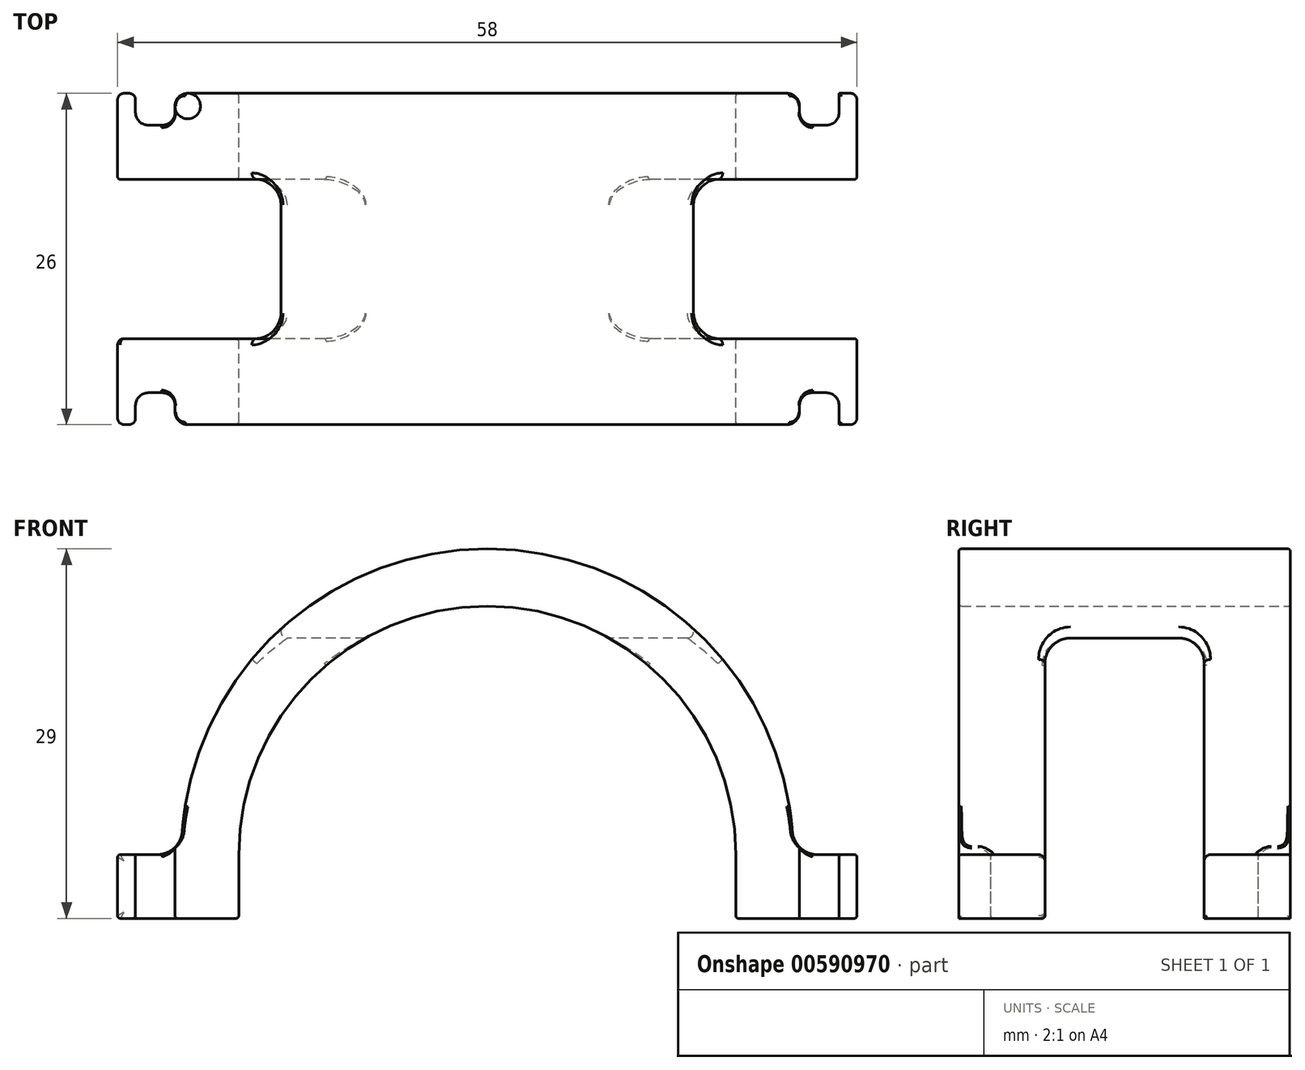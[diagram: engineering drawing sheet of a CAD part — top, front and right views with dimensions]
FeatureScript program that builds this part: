
annotation { "Feature Type Name" : "Feature", "Feature Type Description" : "" }
export const myFeature = defineFeature(function(context is Context, id is Id, definition is map)
    precondition{}
    {
        {
            var Q0;
            Q0=qCreatedBy(makeId("Front.planeOp"),FACE);
            var sketch = newSketch(context, id + "F0", { "sketchPlane" : qUnion([Q0])});
            skArc(sketch, "E0", {"start": v(19.5, 0) * mm, "mid": v(0, 19.5) * mm, "end": v(-19.5, 0) * mm});
            skArc(sketch, "E1", {"start": v(24, 0) * mm, "mid": v(0, 24) * mm, "end": v(-24, 0) * mm});
            skLineSegment(sketch, "E2", {"start": v(-24, 0) * mm, "end": v(24, 0) * mm, "construction": true});
            skLineSegment(sketch, "E3.0", {"start": v(-24, -5) * mm, "end": v(-19.5, -5) * mm});
            skLineSegment(sketch, "E4", {"start": v(-19.5, 0) * mm, "end": v(-19.5, -5) * mm});
            skLineSegment(sketch, "E5", {"start": v(19.5, 0) * mm, "end": v(19.5, -5) * mm});
            skLineSegment(sketch, "E6.trimOffspring", {"start": v(19.5, -5) * mm, "end": v(24, -5) * mm});
            skLineSegment(sketch, "E7", {"start": v(-24, -5) * mm, "end": v(-29, -5) * mm});
            skLineSegment(sketch, "E8", {"start": v(-29, -5) * mm, "end": v(-29, 0) * mm});
            skLineSegment(sketch, "E9", {"start": v(-29, 0) * mm, "end": v(-24, 0) * mm});
            skLineSegment(sketch, "E10.MirrorCS", {"start": v(29, 0) * mm, "end": v(24, 0) * mm});
            skLineSegment(sketch, "E11.MirrorCS", {"start": v(29, -5) * mm, "end": v(29, 0) * mm});
            skLineSegment(sketch, "E12.MirrorCS", {"start": v(24, -5) * mm, "end": v(29, -5) * mm});
            skSolve(sketch);
        }
        {
            var Q0;
            Q0 = qSketchRegion(id + "F0", true);
            extrude(context, id + "F1", {"entities" : qUnion([Q0]), "depth" : 26 * mm, "offsetDistance" : 25 * mm});
        }
        {
            var Q0;
            Q0=makeQuery(id+"F1.opExtrude","SWEPT_FACE",FACE,{"disambiguationData":[OSD([sQuery(id+"F0.wireOp",EDGE,"E9")])]});
            var sketch = newSketch(context, id + "F2", { "sketchPlane" : qUnion([Q0])});
            skLineSegment(sketch, "E13.0", {"start": v(-27.6, -26) * mm, "end": v(-27.6, -23.5) * mm});
            skLineSegment(sketch, "E14.0", {"start": v(-24.5, -26) * mm, "end": v(-24.5, -23.5) * mm});
            skLineSegment(sketch, "E15.0", {"start": v(-27.6, -2.5) * mm, "end": v(-24.5, -2.5) * mm});
            skLineSegment(sketch, "E16", {"start": v(-24, -13) * mm, "end": v(-34.7, -13) * mm, "construction": true});
            skLineSegment(sketch, "E17.MirrorCS", {"start": v(-27.6, -23.5) * mm, "end": v(-24.5, -23.5) * mm});
            skPoint(sketch, "E18.orphan", {"position": v(-29, -2.5) * mm});
            skLineSegment(sketch, "E19.trimOffspring", {"start": v(-27.6, -2.5) * mm, "end": v(-27.6, 0) * mm});
            skPoint(sketch, "E20.orphan", {"position": v(-29, -23.5) * mm});
            skPoint(sketch, "E21.orphan", {"position": v(-24, -23.5) * mm});
            skLineSegment(sketch, "E22.trimOffspring", {"start": v(-24.5, -2.5) * mm, "end": v(-24.5, 0) * mm});
            skLineSegment(sketch, "E23", {"start": v(0, 0) * mm, "end": v(0, -26.74) * mm, "construction": true});
            skLineSegment(sketch, "E24.MirrorCS", {"start": v(27.6, -2.5) * mm, "end": v(24, -2.5) * mm});
            skLineSegment(sketch, "E25.MirrorCS", {"start": v(24.5, -2.5) * mm, "end": v(24.5, 0) * mm});
            skLineSegment(sketch, "E26.MirrorCS", {"start": v(27.6, -2.5) * mm, "end": v(27.6, 0) * mm});
            skLineSegment(sketch, "E27.MirrorCS", {"start": v(27.6, -26) * mm, "end": v(27.6, -23.5) * mm});
            skLineSegment(sketch, "E28.MirrorCS", {"start": v(27.6, -23.5) * mm, "end": v(24.5, -23.5) * mm});
            skLineSegment(sketch, "E29.MirrorCS", {"start": v(24.5, -26) * mm, "end": v(24.5, -23.5) * mm});
            skPoint(sketch, "E30.orphan", {"position": v(-24, -2.5) * mm});
            skLineSegment(sketch, "E31", {"start": v(-27.6, -26) * mm, "end": v(-24.5, -26) * mm});
            skLineSegment(sketch, "E32", {"start": v(-27.6, 0) * mm, "end": v(-24.5, 0) * mm});
            skLineSegment(sketch, "E33", {"start": v(24.5, 0) * mm, "end": v(27.6, 0) * mm});
            skLineSegment(sketch, "E34", {"start": v(27.6, -26) * mm, "end": v(24.5, -26) * mm});
            skSolve(sketch);
        }
        {
            var Q0;
            Q0 = qSketchRegion(id + "F2", true);
            var Q1;
            Q1=makeQuery(id+"F1.opExtrude","SWEPT_FACE",FACE,{"disambiguationData":[OSD([sQuery(id+"F0.wireOp",EDGE,"E6.trimOffspring"),sQuery(id+"F0.wireOp",EDGE,"E12.MirrorCS")])]});
            extrude(context, id + "F3", {"entities" : qUnion([Q0]), "operationType" : NewBodyOperationType.REMOVE, "endBound" : BoundingType.UP_TO_SURFACE, "oppositeDirection" : true, "depth" : 25 * mm, "endBoundEntityFace" : qUnion([Q1]), "offsetDistance" : 25 * mm});
        }
        {
            var Q0;
            Q0=makeQuery(id+"F1.opExtrude","SWEPT_FACE",FACE,{"disambiguationData":[OSD([sQuery(id+"F0.wireOp",EDGE,"E8")])]});
            var sketch = newSketch(context, id + "F4", { "sketchPlane" : qUnion([Q0])});
            skLineSegment(sketch, "E35", {"start": v(13, -5) * mm, "end": v(13, 34.64) * mm, "construction": true});
            skLineSegment(sketch, "E36.0", {"start": v(19.25, -5) * mm, "end": v(19.25, 17) * mm});
            skLineSegment(sketch, "E37.0", {"start": v(19.25, 17) * mm, "end": v(6.75, 17) * mm});
            skLineSegment(sketch, "E38.MirrorCS", {"start": v(6.75, -5) * mm, "end": v(6.75, 17) * mm});
            skLineSegment(sketch, "E39", {"start": v(6.75, -5) * mm, "end": v(19.25, -5) * mm});
            skSolve(sketch);
        }
        {
            var Q0;
            Q0 = qSketchRegion(id + "F4", true);
            extrude(context, id + "F5", {"entities" : qUnion([Q0]), "operationType" : NewBodyOperationType.REMOVE, "endBound" : BoundingType.THROUGH_ALL, "oppositeDirection" : true, "depth" : 25 * mm, "offsetDistance" : 25 * mm});
        }
        {
            var Q0;
            Q0=makeQuery(id+"F3.boolean.opBoolean","COPY",EDGE,{"derivedFrom":makeQuery(id+"F3.opExtrude","SWEPT_EDGE",EDGE,{"disambiguationData":[OSD([sQuery(id+"F2.wireOp",EDGE,"E14.0"),sQuery(id+"F2.wireOp",EDGE,"E17.MirrorCS")])]})});
            var Q1;
            Q1=makeQuery(id+"F3.boolean.opBoolean","COPY",EDGE,{"derivedFrom":makeQuery(id+"F3.opExtrude","SWEPT_EDGE",EDGE,{"disambiguationData":[OSD([sQuery(id+"F2.wireOp",EDGE,"E13.0"),sQuery(id+"F2.wireOp",EDGE,"E17.MirrorCS")])]})});
            var Q2;
            Q2=makeQuery(id+"F3.boolean.opBoolean","COPY",EDGE,{"derivedFrom":makeQuery(id+"F3.opExtrude","SWEPT_EDGE",EDGE,{"disambiguationData":[OSD([sQuery(id+"F2.wireOp",EDGE,"E28.MirrorCS"),sQuery(id+"F2.wireOp",EDGE,"E29.MirrorCS")])]})});
            var Q3;
            Q3=makeQuery(id+"F3.boolean.opBoolean","COPY",EDGE,{"derivedFrom":makeQuery(id+"F3.opExtrude","SWEPT_EDGE",EDGE,{"disambiguationData":[OSD([sQuery(id+"F2.wireOp",EDGE,"E27.MirrorCS"),sQuery(id+"F2.wireOp",EDGE,"E28.MirrorCS")])]})});
            var Q4;
            Q4=makeQuery(id+"F3.boolean.opBoolean","COPY",EDGE,{"derivedFrom":makeQuery(id+"F3.opExtrude","SWEPT_EDGE",EDGE,{"disambiguationData":[OSD([sQuery(id+"F2.wireOp",EDGE,"E15.0"),sQuery(id+"F2.wireOp",EDGE,"E22.trimOffspring")])]})});
            var Q5;
            Q5=makeQuery(id+"F3.boolean.opBoolean","COPY",EDGE,{"derivedFrom":makeQuery(id+"F3.opExtrude","SWEPT_EDGE",EDGE,{"disambiguationData":[OSD([sQuery(id+"F2.wireOp",EDGE,"E24.MirrorCS"),sQuery(id+"F2.wireOp",EDGE,"E26.MirrorCS")])]})});
            var Q6;
            Q6=makeQuery(id+"F3.boolean.opBoolean","COPY",EDGE,{"derivedFrom":makeQuery(id+"F3.opExtrude","SWEPT_EDGE",EDGE,{"disambiguationData":[OSD([sQuery(id+"F2.wireOp",EDGE,"E15.0"),sQuery(id+"F2.wireOp",EDGE,"E19.trimOffspring")])]})});
            var Q7;
            Q7=makeQuery(id+"F3.boolean.opBoolean","COPY",EDGE,{"derivedFrom":makeQuery(id+"F3.opExtrude","SWEPT_EDGE",EDGE,{"disambiguationData":[OSD([sQuery(id+"F2.wireOp",EDGE,"E24.MirrorCS"),sQuery(id+"F2.wireOp",EDGE,"E25.MirrorCS")])]})});
            var Q8;
            Q8=makeQuery(id+"F3.boolean.opBoolean","COPY",EDGE,{"derivedFrom":makeQuery(id+"F3.opExtrude","SWEPT_EDGE",EDGE,{"disambiguationData":[OSD([sQuery(id+"F0.wireOp",EDGE,"E9"),sQuery(id+"F2.wireOp",EDGE,"E14.0"),sQuery(id+"F2.wireOp",EDGE,"E31")])]})});
            var Q9;
            Q9=makeQuery(id+"F3.boolean.opBoolean","COPY",EDGE,{"derivedFrom":makeQuery(id+"F3.opExtrude","SWEPT_EDGE",EDGE,{"disambiguationData":[OSD([sQuery(id+"F0.wireOp",EDGE,"E9"),sQuery(id+"F2.wireOp",EDGE,"E22.trimOffspring"),sQuery(id+"F2.wireOp",EDGE,"E32")])]})});
            var Q10;
            Q10=makeQuery(id+"F3.boolean.opBoolean","COPY",EDGE,{"derivedFrom":makeQuery(id+"F3.opExtrude","SWEPT_EDGE",EDGE,{"disambiguationData":[OSD([sQuery(id+"F2.wireOp",EDGE,"E29.MirrorCS"),sQuery(id+"F2.wireOp",EDGE,"E34")])]})});
            var Q11;
            Q11=makeQuery(id+"F3.boolean.opBoolean","COPY",EDGE,{"derivedFrom":makeQuery(id+"F3.opExtrude","SWEPT_EDGE",EDGE,{"disambiguationData":[OSD([sQuery(id+"F2.wireOp",EDGE,"E25.MirrorCS"),sQuery(id+"F2.wireOp",EDGE,"E33")])]})});
            fillet(context, id + "F6", {"entities" : qUnion([Q0, Q1, Q2, Q3, Q4, Q5, Q6, Q7, Q8, Q9, Q10, Q11]), "radius" : 1 * mm, "tangentPropagation" : true, "allowEdgeOverflow" : false});
        }
        {
            var Q0;
            Q0=makeQuery(id+"F3.boolean.opBoolean","COPY",EDGE,{"derivedFrom":makeQuery(id+"F3.opExtrude","SWEPT_EDGE",EDGE,{"disambiguationData":[OSD([sQuery(id+"F2.wireOp",EDGE,"E26.MirrorCS"),sQuery(id+"F2.wireOp",EDGE,"E33")])]})});
            var Q1;
            Q1=makeQuery(id+"F1.opExtrude","CAP_EDGE",EDGE,{"disambiguationData":[OSD([sQuery(id+"F0.wireOp",EDGE,"E11.MirrorCS")])],"isStart":true});
            var Q2;
            Q2=makeQuery(id+"F1.opExtrude","CAP_EDGE",EDGE,{"disambiguationData":[OSD([sQuery(id+"F0.wireOp",EDGE,"E11.MirrorCS")])],"isStart":false});
            var Q3;
            Q3=makeQuery(id+"F3.boolean.opBoolean","COPY",EDGE,{"derivedFrom":makeQuery(id+"F3.opExtrude","SWEPT_EDGE",EDGE,{"disambiguationData":[OSD([sQuery(id+"F2.wireOp",EDGE,"E27.MirrorCS"),sQuery(id+"F2.wireOp",EDGE,"E34")])]})});
            var Q4;
            Q4=makeQuery(id+"F3.boolean.opBoolean","COPY",EDGE,{"derivedFrom":makeQuery(id+"F3.opExtrude","SWEPT_EDGE",EDGE,{"disambiguationData":[OSD([sQuery(id+"F0.wireOp",EDGE,"E9"),sQuery(id+"F2.wireOp",EDGE,"E13.0"),sQuery(id+"F2.wireOp",EDGE,"E31")])]})});
            var Q5;
            Q5=makeQuery(id+"F1.opExtrude","CAP_EDGE",EDGE,{"disambiguationData":[OSD([sQuery(id+"F0.wireOp",EDGE,"E8")])],"isStart":false});
            var Q6;
            Q6=makeQuery(id+"F1.opExtrude","CAP_EDGE",EDGE,{"disambiguationData":[OSD([sQuery(id+"F0.wireOp",EDGE,"E8")])],"isStart":true});
            var Q7;
            Q7=makeQuery(id+"F3.boolean.opBoolean","COPY",EDGE,{"derivedFrom":makeQuery(id+"F3.opExtrude","SWEPT_EDGE",EDGE,{"disambiguationData":[OSD([sQuery(id+"F0.wireOp",EDGE,"E9"),sQuery(id+"F2.wireOp",EDGE,"E19.trimOffspring"),sQuery(id+"F2.wireOp",EDGE,"E32")])]})});
            fillet(context, id + "F7", {"entities" : qUnion([Q0, Q1, Q2, Q3, Q4, Q5, Q6, Q7]), "radius" : 0.5 * mm, "tangentPropagation" : true, "allowEdgeOverflow" : false});
        }
        {
            var Q0;
            {var subQ0=sQuery(id+"F0.wireOp",EDGE,"E10.MirrorCS");var subQ1=sQuery(id+"F0.wireOp",EDGE,"E1");Q0=makeQuery(id+"F5.boolean.opBoolean","SPLIT",EDGE,{"disambiguationData":[TD([makeQuery(id+"F5.opExtrude","SWEPT_FACE",FACE,{"disambiguationData":[OSD([sQuery(id+"F4.wireOp",EDGE,"E36.0")])]})])],"derivedFrom":makeQuery(id+"F1.opExtrude","SWEPT_EDGE",EDGE,{"disambiguationData":[OSD([subQ1,subQ0])]})});}
            var Q1;
            {var subQ0=sQuery(id+"F0.wireOp",EDGE,"E10.MirrorCS");var subQ1=sQuery(id+"F0.wireOp",EDGE,"E1");Q1=makeQuery(id+"F5.boolean.opBoolean","SPLIT",EDGE,{"disambiguationData":[TD([makeQuery(id+"F5.opExtrude","SWEPT_FACE",FACE,{"disambiguationData":[OSD([sQuery(id+"F4.wireOp",EDGE,"E38.MirrorCS")])]})])],"derivedFrom":makeQuery(id+"F1.opExtrude","SWEPT_EDGE",EDGE,{"disambiguationData":[OSD([subQ1,subQ0])]})});}
            var Q2;
            {var subQ0=sQuery(id+"F0.wireOp",EDGE,"E9");var subQ1=sQuery(id+"F0.wireOp",EDGE,"E1");Q2=makeQuery(id+"F5.boolean.opBoolean","SPLIT",EDGE,{"disambiguationData":[TD([makeQuery(id+"F5.opExtrude","SWEPT_FACE",FACE,{"disambiguationData":[OSD([sQuery(id+"F4.wireOp",EDGE,"E36.0")])]})])],"derivedFrom":makeQuery(id+"F1.opExtrude","SWEPT_EDGE",EDGE,{"disambiguationData":[OSD([subQ1,subQ0])]})});}
            var Q3;
            {var subQ0=sQuery(id+"F0.wireOp",EDGE,"E9");var subQ1=sQuery(id+"F0.wireOp",EDGE,"E1");Q3=makeQuery(id+"F5.boolean.opBoolean","SPLIT",EDGE,{"disambiguationData":[TD([makeQuery(id+"F5.opExtrude","SWEPT_FACE",FACE,{"disambiguationData":[OSD([sQuery(id+"F4.wireOp",EDGE,"E38.MirrorCS")])]})])],"derivedFrom":makeQuery(id+"F1.opExtrude","SWEPT_EDGE",EDGE,{"disambiguationData":[OSD([subQ1,subQ0])]})});}
            var Q4;
            Q4=makeQuery(id+"F5.boolean.opBoolean","COPY",EDGE,{"disambiguationData":[OD(1.0)],"derivedFrom":makeQuery(id+"F5.opExtrude","SWEPT_EDGE",EDGE,{"disambiguationData":[OSD([sQuery(id+"F4.wireOp",EDGE,"E36.0"),sQuery(id+"F4.wireOp",EDGE,"E37.0")])]})});
            var Q5;
            Q5=makeQuery(id+"F5.boolean.opBoolean","COPY",EDGE,{"disambiguationData":[OD(1.0)],"derivedFrom":makeQuery(id+"F5.opExtrude","SWEPT_EDGE",EDGE,{"disambiguationData":[OSD([sQuery(id+"F4.wireOp",EDGE,"E37.0"),sQuery(id+"F4.wireOp",EDGE,"E38.MirrorCS")])]})});
            var Q6;
            Q6=makeQuery(id+"F5.boolean.opBoolean","COPY",EDGE,{"disambiguationData":[OD(0.0)],"derivedFrom":makeQuery(id+"F5.opExtrude","SWEPT_EDGE",EDGE,{"disambiguationData":[OSD([sQuery(id+"F4.wireOp",EDGE,"E37.0"),sQuery(id+"F4.wireOp",EDGE,"E38.MirrorCS")])]})});
            var Q7;
            Q7=makeQuery(id+"F5.boolean.opBoolean","COPY",EDGE,{"disambiguationData":[OD(0.0)],"derivedFrom":makeQuery(id+"F5.opExtrude","SWEPT_EDGE",EDGE,{"disambiguationData":[OSD([sQuery(id+"F4.wireOp",EDGE,"E36.0"),sQuery(id+"F4.wireOp",EDGE,"E37.0")])]})});
            fillet(context, id + "F8", {"entities" : qUnion([Q0, Q1, Q2, Q3, Q4, Q5, Q6, Q7]), "radius" : 2 * mm, "tangentPropagation" : true, "allowEdgeOverflow" : false});
        }
        {
            var Q0;
            Q0=makeQuery(id+"F5.boolean.opBoolean","INTERSECT",EDGE,{"derivedFrom":[makeQuery(id+"F1.opExtrude","SWEPT_FACE",FACE,{"disambiguationData":[OSD([sQuery(id+"F0.wireOp",EDGE,"E11.MirrorCS")])]}),makeQuery(id+"F5.opExtrude","SWEPT_FACE",FACE,{"disambiguationData":[OSD([sQuery(id+"F4.wireOp",EDGE,"E36.0")])]})]});
            var Q1;
            Q1=makeQuery(id+"F5.boolean.opBoolean","INTERSECT",EDGE,{"derivedFrom":[makeQuery(id+"F1.opExtrude","SWEPT_FACE",FACE,{"disambiguationData":[OSD([sQuery(id+"F0.wireOp",EDGE,"E11.MirrorCS")])]}),makeQuery(id+"F5.opExtrude","SWEPT_FACE",FACE,{"disambiguationData":[OSD([sQuery(id+"F4.wireOp",EDGE,"E38.MirrorCS")])]})]});
            var Q2;
            {var subQ0=sQuery(id+"F4.wireOp",EDGE,"E38.MirrorCS");Q2=makeQuery(id+"F5.boolean.opBoolean","COPY",EDGE,{"disambiguationData":[topologyDisambiguationEdgeConnected([makeQuery(id+"F1.opExtrude","SWEPT_FACE",FACE,{"disambiguationData":[OSD([sQuery(id+"F0.wireOp",EDGE,"E6.trimOffspring"),sQuery(id+"F0.wireOp",EDGE,"E12.MirrorCS")])]})])],"derivedFrom":makeQuery(id+"F5.opExtrude","SWEPT_EDGE",EDGE,{"disambiguationData":[OSD([sQuery(id+"F0.wireOp",EDGE,"E7"),sQuery(id+"F0.wireOp",EDGE,"E8"),subQ0,sQuery(id+"F4.wireOp",EDGE,"E39")])]})});}
            var Q3;
            {var subQ0=sQuery(id+"F4.wireOp",EDGE,"E36.0");Q3=makeQuery(id+"F5.boolean.opBoolean","COPY",EDGE,{"disambiguationData":[topologyDisambiguationEdgeConnected([makeQuery(id+"F1.opExtrude","SWEPT_FACE",FACE,{"disambiguationData":[OSD([sQuery(id+"F0.wireOp",EDGE,"E6.trimOffspring"),sQuery(id+"F0.wireOp",EDGE,"E12.MirrorCS")])]})])],"derivedFrom":makeQuery(id+"F5.opExtrude","SWEPT_EDGE",EDGE,{"disambiguationData":[OSD([sQuery(id+"F0.wireOp",EDGE,"E7"),sQuery(id+"F0.wireOp",EDGE,"E8"),subQ0,sQuery(id+"F4.wireOp",EDGE,"E39")])]})});}
            var Q4;
            Q4=makeQuery(id+"F5.boolean.opBoolean","COPY",EDGE,{"derivedFrom":makeQuery(id+"F5.opExtrude","CAP_EDGE",EDGE,{"disambiguationData":[OSD([sQuery(id+"F4.wireOp",EDGE,"E38.MirrorCS")])],"isStart":true})});
            var Q5;
            Q5=makeQuery(id+"F5.boolean.opBoolean","COPY",EDGE,{"derivedFrom":makeQuery(id+"F5.opExtrude","CAP_EDGE",EDGE,{"disambiguationData":[OSD([sQuery(id+"F4.wireOp",EDGE,"E36.0")])],"isStart":true})});
            var Q6;
            {var subQ0=sQuery(id+"F0.wireOp",EDGE,"E7");var subQ1=sQuery(id+"F4.wireOp",EDGE,"E38.MirrorCS");Q6=makeQuery(id+"F5.boolean.opBoolean","COPY",EDGE,{"disambiguationData":[topologyDisambiguationEdgeConnected([makeQuery(id+"F1.opExtrude","SWEPT_FACE",FACE,{"disambiguationData":[OSD([sQuery(id+"F0.wireOp",EDGE,"E3.0"),subQ0])]})])],"derivedFrom":makeQuery(id+"F5.opExtrude","SWEPT_EDGE",EDGE,{"disambiguationData":[OSD([subQ0,sQuery(id+"F0.wireOp",EDGE,"E8"),subQ1,sQuery(id+"F4.wireOp",EDGE,"E39")])]})});}
            var Q7;
            {var subQ0=sQuery(id+"F0.wireOp",EDGE,"E7");var subQ1=sQuery(id+"F4.wireOp",EDGE,"E36.0");Q7=makeQuery(id+"F5.boolean.opBoolean","COPY",EDGE,{"disambiguationData":[topologyDisambiguationEdgeConnected([makeQuery(id+"F1.opExtrude","SWEPT_FACE",FACE,{"disambiguationData":[OSD([sQuery(id+"F0.wireOp",EDGE,"E3.0"),subQ0])]})])],"derivedFrom":makeQuery(id+"F5.opExtrude","SWEPT_EDGE",EDGE,{"disambiguationData":[OSD([subQ0,sQuery(id+"F0.wireOp",EDGE,"E8"),subQ1,sQuery(id+"F4.wireOp",EDGE,"E39")])]})});}
            var Q8;
            {var subQ0=sQuery(id+"F0.wireOp",EDGE,"E9");var subQ1=sQuery(id+"F0.wireOp",EDGE,"E8");Q8=makeQuery(id+"F5.boolean.opBoolean","SPLIT",EDGE,{"disambiguationData":[TD([makeQuery(id+"F5.opExtrude","SWEPT_FACE",FACE,{"disambiguationData":[OSD([sQuery(id+"F4.wireOp",EDGE,"E38.MirrorCS")])]})])],"derivedFrom":makeQuery(id+"F1.opExtrude","SWEPT_EDGE",EDGE,{"disambiguationData":[OSD([subQ1,subQ0])]})});}
            var Q9;
            {var subQ0=sQuery(id+"F0.wireOp",EDGE,"E9");var subQ1=sQuery(id+"F0.wireOp",EDGE,"E8");Q9=makeQuery(id+"F5.boolean.opBoolean","SPLIT",EDGE,{"disambiguationData":[TD([makeQuery(id+"F5.opExtrude","SWEPT_FACE",FACE,{"disambiguationData":[OSD([sQuery(id+"F4.wireOp",EDGE,"E36.0")])]})])],"derivedFrom":makeQuery(id+"F1.opExtrude","SWEPT_EDGE",EDGE,{"disambiguationData":[OSD([subQ1,subQ0])]})});}
            var Q10;
            {var subQ0=sQuery(id+"F0.wireOp",EDGE,"E8");var subQ1=sQuery(id+"F0.wireOp",EDGE,"E7");Q10=makeQuery(id+"F5.boolean.opBoolean","SPLIT",EDGE,{"disambiguationData":[TD([makeQuery(id+"F5.opExtrude","SWEPT_FACE",FACE,{"disambiguationData":[OSD([sQuery(id+"F4.wireOp",EDGE,"E38.MirrorCS")])]})])],"derivedFrom":makeQuery(id+"F1.opExtrude","SWEPT_EDGE",EDGE,{"disambiguationData":[OSD([subQ1,subQ0])]})});}
            var Q11;
            {var subQ0=sQuery(id+"F0.wireOp",EDGE,"E8");var subQ1=sQuery(id+"F0.wireOp",EDGE,"E7");Q11=makeQuery(id+"F5.boolean.opBoolean","SPLIT",EDGE,{"disambiguationData":[TD([makeQuery(id+"F5.opExtrude","SWEPT_FACE",FACE,{"disambiguationData":[OSD([sQuery(id+"F4.wireOp",EDGE,"E36.0")])]})])],"derivedFrom":makeQuery(id+"F1.opExtrude","SWEPT_EDGE",EDGE,{"disambiguationData":[OSD([subQ1,subQ0])]})});}
            var Q12;
            {var subQ1=sQuery(id+"F0.wireOp",EDGE,"E4");var subQ2=sQuery(id+"F0.wireOp",EDGE,"E3.0");Q12=makeQuery(id+"F5.boolean.opBoolean","SPLIT",EDGE,{"disambiguationData":[TD([makeQuery(id+"F5.opExtrude","SWEPT_FACE",FACE,{"disambiguationData":[OSD([sQuery(id+"F4.wireOp",EDGE,"E38.MirrorCS")])]})])],"derivedFrom":makeQuery(id+"F1.opExtrude","SWEPT_EDGE",EDGE,{"disambiguationData":[OSD([subQ2,subQ1])]})});}
            var Q13;
            {var subQ1=sQuery(id+"F0.wireOp",EDGE,"E4");var subQ2=sQuery(id+"F0.wireOp",EDGE,"E3.0");Q13=makeQuery(id+"F5.boolean.opBoolean","SPLIT",EDGE,{"disambiguationData":[TD([makeQuery(id+"F5.opExtrude","SWEPT_FACE",FACE,{"disambiguationData":[OSD([sQuery(id+"F4.wireOp",EDGE,"E36.0")])]})])],"derivedFrom":makeQuery(id+"F1.opExtrude","SWEPT_EDGE",EDGE,{"disambiguationData":[OSD([subQ2,subQ1])]})});}
            var Q14;
            {var subQ1=sQuery(id+"F0.wireOp",EDGE,"E6.trimOffspring");var subQ2=sQuery(id+"F0.wireOp",EDGE,"E5");Q14=makeQuery(id+"F5.boolean.opBoolean","SPLIT",EDGE,{"disambiguationData":[TD([makeQuery(id+"F5.opExtrude","SWEPT_FACE",FACE,{"disambiguationData":[OSD([sQuery(id+"F4.wireOp",EDGE,"E38.MirrorCS")])]})])],"derivedFrom":makeQuery(id+"F1.opExtrude","SWEPT_EDGE",EDGE,{"disambiguationData":[OSD([subQ2,subQ1])]})});}
            var Q15;
            {var subQ0=sQuery(id+"F0.wireOp",EDGE,"E12.MirrorCS");var subQ1=sQuery(id+"F0.wireOp",EDGE,"E11.MirrorCS");Q15=makeQuery(id+"F5.boolean.opBoolean","SPLIT",EDGE,{"disambiguationData":[TD([makeQuery(id+"F5.opExtrude","SWEPT_FACE",FACE,{"disambiguationData":[OSD([sQuery(id+"F4.wireOp",EDGE,"E38.MirrorCS")])]})])],"derivedFrom":makeQuery(id+"F1.opExtrude","SWEPT_EDGE",EDGE,{"disambiguationData":[OSD([subQ1,subQ0])]})});}
            var Q16;
            {var subQ0=sQuery(id+"F0.wireOp",EDGE,"E12.MirrorCS");var subQ1=sQuery(id+"F0.wireOp",EDGE,"E11.MirrorCS");Q16=makeQuery(id+"F5.boolean.opBoolean","SPLIT",EDGE,{"disambiguationData":[TD([makeQuery(id+"F5.opExtrude","SWEPT_FACE",FACE,{"disambiguationData":[OSD([sQuery(id+"F4.wireOp",EDGE,"E36.0")])]})])],"derivedFrom":makeQuery(id+"F1.opExtrude","SWEPT_EDGE",EDGE,{"disambiguationData":[OSD([subQ1,subQ0])]})});}
            var Q17;
            {var subQ1=sQuery(id+"F0.wireOp",EDGE,"E6.trimOffspring");var subQ2=sQuery(id+"F0.wireOp",EDGE,"E5");Q17=makeQuery(id+"F5.boolean.opBoolean","SPLIT",EDGE,{"disambiguationData":[TD([makeQuery(id+"F5.opExtrude","SWEPT_FACE",FACE,{"disambiguationData":[OSD([sQuery(id+"F4.wireOp",EDGE,"E36.0")])]})])],"derivedFrom":makeQuery(id+"F1.opExtrude","SWEPT_EDGE",EDGE,{"disambiguationData":[OSD([subQ2,subQ1])]})});}
            var Q18;
            {var subQ0=sQuery(id+"F0.wireOp",EDGE,"E11.MirrorCS");var subQ1=sQuery(id+"F0.wireOp",EDGE,"E10.MirrorCS");Q18=makeQuery(id+"F5.boolean.opBoolean","SPLIT",EDGE,{"disambiguationData":[TD([makeQuery(id+"F5.opExtrude","SWEPT_FACE",FACE,{"disambiguationData":[OSD([sQuery(id+"F4.wireOp",EDGE,"E38.MirrorCS")])]})])],"derivedFrom":makeQuery(id+"F1.opExtrude","SWEPT_EDGE",EDGE,{"disambiguationData":[OSD([subQ1,subQ0])]})});}
            var Q19;
            {var subQ0=sQuery(id+"F0.wireOp",EDGE,"E11.MirrorCS");var subQ1=sQuery(id+"F0.wireOp",EDGE,"E10.MirrorCS");Q19=makeQuery(id+"F5.boolean.opBoolean","SPLIT",EDGE,{"disambiguationData":[TD([makeQuery(id+"F5.opExtrude","SWEPT_FACE",FACE,{"disambiguationData":[OSD([sQuery(id+"F4.wireOp",EDGE,"E36.0")])]})])],"derivedFrom":makeQuery(id+"F1.opExtrude","SWEPT_EDGE",EDGE,{"disambiguationData":[OSD([subQ1,subQ0])]})});}
            var Q20;
            Q20=makeQuery(id+"F1.opExtrude","SWEPT_FACE",FACE,{"disambiguationData":[OSD([sQuery(id+"F0.wireOp",EDGE,"E0")])]});
            fillet(context, id + "F9", {"entities" : qUnion([Q0, Q1, Q2, Q3, Q4, Q5, Q6, Q7, Q8, Q9, Q10, Q11, Q12, Q13, Q14, Q15, Q16, Q17, Q18, Q19, Q20]), "radius" : .2 * mm, "tangentPropagation" : true, "allowEdgeOverflow" : false});
        }
        {
            var Q0;
            Q0=makeQuery(id+"F5.boolean.opBoolean","INTERSECT",EDGE,{"disambiguationData":[OD(0.0)],"derivedFrom":[makeQuery(id+"F1.opExtrude","SWEPT_FACE",FACE,{"disambiguationData":[OSD([sQuery(id+"F0.wireOp",EDGE,"E1")])]}),makeQuery(id+"F5.opExtrude","SWEPT_FACE",FACE,{"disambiguationData":[OSD([sQuery(id+"F4.wireOp",EDGE,"E38.MirrorCS")])]})]});
            var Q1;
            Q1=makeQuery(id+"F8.opFillet","BLEND_EDGE",EDGE,{"blendedFrom":[makeQuery(id+"F5.boolean.opBoolean","COPY",EDGE,{"disambiguationData":[OD(0.0)],"derivedFrom":makeQuery(id+"F5.opExtrude","SWEPT_EDGE",EDGE,{"disambiguationData":[OSD([sQuery(id+"F4.wireOp",EDGE,"E37.0"),sQuery(id+"F4.wireOp",EDGE,"E38.MirrorCS")])]})}),makeQuery(id+"F1.opExtrude","SWEPT_FACE",FACE,{"disambiguationData":[OSD([sQuery(id+"F0.wireOp",EDGE,"E1")])]})],"blendedInto":[makeQuery(id+"F1.opExtrude","SWEPT_FACE",FACE,{"disambiguationData":[OSD([sQuery(id+"F0.wireOp",EDGE,"E1")])]})]});
            var Q2;
            Q2=makeQuery(id+"F5.boolean.opBoolean","INTERSECT",EDGE,{"disambiguationData":[OD(0.0)],"derivedFrom":[makeQuery(id+"F1.opExtrude","SWEPT_FACE",FACE,{"disambiguationData":[OSD([sQuery(id+"F0.wireOp",EDGE,"E1")])]}),makeQuery(id+"F5.opExtrude","SWEPT_FACE",FACE,{"disambiguationData":[OSD([sQuery(id+"F4.wireOp",EDGE,"E37.0")])]})]});
            var Q3;
            Q3=makeQuery(id+"F8.opFillet","BLEND_EDGE",EDGE,{"blendedFrom":[makeQuery(id+"F5.boolean.opBoolean","COPY",EDGE,{"disambiguationData":[OD(0.0)],"derivedFrom":makeQuery(id+"F5.opExtrude","SWEPT_EDGE",EDGE,{"disambiguationData":[OSD([sQuery(id+"F4.wireOp",EDGE,"E36.0"),sQuery(id+"F4.wireOp",EDGE,"E37.0")])]})}),makeQuery(id+"F1.opExtrude","SWEPT_FACE",FACE,{"disambiguationData":[OSD([sQuery(id+"F0.wireOp",EDGE,"E1")])]})],"blendedInto":[makeQuery(id+"F1.opExtrude","SWEPT_FACE",FACE,{"disambiguationData":[OSD([sQuery(id+"F0.wireOp",EDGE,"E1")])]})]});
            var Q4;
            Q4=makeQuery(id+"F5.boolean.opBoolean","INTERSECT",EDGE,{"disambiguationData":[OD(0.0)],"derivedFrom":[makeQuery(id+"F1.opExtrude","SWEPT_FACE",FACE,{"disambiguationData":[OSD([sQuery(id+"F0.wireOp",EDGE,"E1")])]}),makeQuery(id+"F5.opExtrude","SWEPT_FACE",FACE,{"disambiguationData":[OSD([sQuery(id+"F4.wireOp",EDGE,"E36.0")])]})]});
            var Q5;
            {var subQ2=sQuery(id+"F0.wireOp",EDGE,"E1");var subQ4=sQuery(id+"F0.wireOp",EDGE,"E4");var subQ7=sQuery(id+"F0.wireOp",EDGE,"E9");var subQ9=makeQuery(id+"F5.opExtrude","SWEPT_FACE",FACE,{"disambiguationData":[OSD([sQuery(id+"F4.wireOp",EDGE,"E38.MirrorCS")])]});Q5=makeQuery(id+"F8.opFillet","BLEND_EDGE",EDGE,{"blendedFrom":[makeQuery(id+"F5.boolean.opBoolean","SPLIT",EDGE,{"disambiguationData":[TD([subQ9])],"derivedFrom":makeQuery(id+"F1.opExtrude","SWEPT_EDGE",EDGE,{"disambiguationData":[OSD([subQ2,subQ7])]})}),makeQuery(id+"F5.boolean.opBoolean","COPY",FACE,{"disambiguationData":[TD([makeQuery(id+"F1.opExtrude","SWEPT_FACE",FACE,{"disambiguationData":[OSD([subQ4])]})])],"derivedFrom":subQ9})],"blendedInto":[makeQuery(id+"F5.boolean.opBoolean","COPY",FACE,{"disambiguationData":[TD([makeQuery(id+"F1.opExtrude","SWEPT_FACE",FACE,{"disambiguationData":[OSD([subQ4])]})])],"derivedFrom":subQ9})]});}
            var Q6;
            Q6=makeQuery(id+"F5.boolean.opBoolean","INTERSECT",EDGE,{"derivedFrom":[makeQuery(id+"F1.opExtrude","SWEPT_FACE",FACE,{"disambiguationData":[OSD([sQuery(id+"F0.wireOp",EDGE,"E9")])]}),makeQuery(id+"F5.opExtrude","SWEPT_FACE",FACE,{"disambiguationData":[OSD([sQuery(id+"F4.wireOp",EDGE,"E38.MirrorCS")])]})]});
            var Q7;
            {var subQ2=sQuery(id+"F0.wireOp",EDGE,"E1");var subQ4=sQuery(id+"F0.wireOp",EDGE,"E4");var subQ7=sQuery(id+"F0.wireOp",EDGE,"E9");var subQ9=makeQuery(id+"F5.opExtrude","SWEPT_FACE",FACE,{"disambiguationData":[OSD([sQuery(id+"F4.wireOp",EDGE,"E36.0")])]});Q7=makeQuery(id+"F8.opFillet","BLEND_EDGE",EDGE,{"blendedFrom":[makeQuery(id+"F5.boolean.opBoolean","SPLIT",EDGE,{"disambiguationData":[TD([subQ9])],"derivedFrom":makeQuery(id+"F1.opExtrude","SWEPT_EDGE",EDGE,{"disambiguationData":[OSD([subQ2,subQ7])]})}),makeQuery(id+"F5.boolean.opBoolean","COPY",FACE,{"disambiguationData":[TD([makeQuery(id+"F1.opExtrude","SWEPT_FACE",FACE,{"disambiguationData":[OSD([subQ4])]})])],"derivedFrom":subQ9})],"blendedInto":[makeQuery(id+"F5.boolean.opBoolean","COPY",FACE,{"disambiguationData":[TD([makeQuery(id+"F1.opExtrude","SWEPT_FACE",FACE,{"disambiguationData":[OSD([subQ4])]})])],"derivedFrom":subQ9})]});}
            var Q8;
            Q8=makeQuery(id+"F5.boolean.opBoolean","INTERSECT",EDGE,{"derivedFrom":[makeQuery(id+"F1.opExtrude","SWEPT_FACE",FACE,{"disambiguationData":[OSD([sQuery(id+"F0.wireOp",EDGE,"E9")])]}),makeQuery(id+"F5.opExtrude","SWEPT_FACE",FACE,{"disambiguationData":[OSD([sQuery(id+"F4.wireOp",EDGE,"E36.0")])]})]});
            var Q9;
            Q9=makeQuery(id+"F5.boolean.opBoolean","INTERSECT",EDGE,{"derivedFrom":[makeQuery(id+"F1.opExtrude","SWEPT_FACE",FACE,{"disambiguationData":[OSD([sQuery(id+"F0.wireOp",EDGE,"E10.MirrorCS")])]}),makeQuery(id+"F5.opExtrude","SWEPT_FACE",FACE,{"disambiguationData":[OSD([sQuery(id+"F4.wireOp",EDGE,"E36.0")])]})]});
            var Q10;
            {var subQ2=sQuery(id+"F0.wireOp",EDGE,"E5");var subQ3=sQuery(id+"F0.wireOp",EDGE,"E1");var subQ7=sQuery(id+"F0.wireOp",EDGE,"E10.MirrorCS");var subQ9=makeQuery(id+"F5.opExtrude","SWEPT_FACE",FACE,{"disambiguationData":[OSD([sQuery(id+"F4.wireOp",EDGE,"E36.0")])]});Q10=makeQuery(id+"F8.opFillet","BLEND_EDGE",EDGE,{"blendedFrom":[makeQuery(id+"F5.boolean.opBoolean","SPLIT",EDGE,{"disambiguationData":[TD([subQ9])],"derivedFrom":makeQuery(id+"F1.opExtrude","SWEPT_EDGE",EDGE,{"disambiguationData":[OSD([subQ3,subQ7])]})}),makeQuery(id+"F5.boolean.opBoolean","COPY",FACE,{"disambiguationData":[TD([makeQuery(id+"F1.opExtrude","SWEPT_FACE",FACE,{"disambiguationData":[OSD([subQ2])]})])],"derivedFrom":subQ9})],"blendedInto":[makeQuery(id+"F5.boolean.opBoolean","COPY",FACE,{"disambiguationData":[TD([makeQuery(id+"F1.opExtrude","SWEPT_FACE",FACE,{"disambiguationData":[OSD([subQ2])]})])],"derivedFrom":subQ9})]});}
            var Q11;
            Q11=makeQuery(id+"F5.boolean.opBoolean","INTERSECT",EDGE,{"disambiguationData":[OD(1.0)],"derivedFrom":[makeQuery(id+"F1.opExtrude","SWEPT_FACE",FACE,{"disambiguationData":[OSD([sQuery(id+"F0.wireOp",EDGE,"E1")])]}),makeQuery(id+"F5.opExtrude","SWEPT_FACE",FACE,{"disambiguationData":[OSD([sQuery(id+"F4.wireOp",EDGE,"E36.0")])]})]});
            var Q12;
            Q12=makeQuery(id+"F8.opFillet","BLEND_EDGE",EDGE,{"blendedFrom":[makeQuery(id+"F5.boolean.opBoolean","COPY",EDGE,{"disambiguationData":[OD(1.0)],"derivedFrom":makeQuery(id+"F5.opExtrude","SWEPT_EDGE",EDGE,{"disambiguationData":[OSD([sQuery(id+"F4.wireOp",EDGE,"E36.0"),sQuery(id+"F4.wireOp",EDGE,"E37.0")])]})}),makeQuery(id+"F1.opExtrude","SWEPT_FACE",FACE,{"disambiguationData":[OSD([sQuery(id+"F0.wireOp",EDGE,"E1")])]})],"blendedInto":[makeQuery(id+"F1.opExtrude","SWEPT_FACE",FACE,{"disambiguationData":[OSD([sQuery(id+"F0.wireOp",EDGE,"E1")])]})]});
            var Q13;
            Q13=makeQuery(id+"F5.boolean.opBoolean","INTERSECT",EDGE,{"disambiguationData":[OD(1.0)],"derivedFrom":[makeQuery(id+"F1.opExtrude","SWEPT_FACE",FACE,{"disambiguationData":[OSD([sQuery(id+"F0.wireOp",EDGE,"E1")])]}),makeQuery(id+"F5.opExtrude","SWEPT_FACE",FACE,{"disambiguationData":[OSD([sQuery(id+"F4.wireOp",EDGE,"E37.0")])]})]});
            var Q14;
            Q14=makeQuery(id+"F8.opFillet","BLEND_EDGE",EDGE,{"blendedFrom":[makeQuery(id+"F5.boolean.opBoolean","COPY",EDGE,{"disambiguationData":[OD(1.0)],"derivedFrom":makeQuery(id+"F5.opExtrude","SWEPT_EDGE",EDGE,{"disambiguationData":[OSD([sQuery(id+"F4.wireOp",EDGE,"E37.0"),sQuery(id+"F4.wireOp",EDGE,"E38.MirrorCS")])]})}),makeQuery(id+"F1.opExtrude","SWEPT_FACE",FACE,{"disambiguationData":[OSD([sQuery(id+"F0.wireOp",EDGE,"E1")])]})],"blendedInto":[makeQuery(id+"F1.opExtrude","SWEPT_FACE",FACE,{"disambiguationData":[OSD([sQuery(id+"F0.wireOp",EDGE,"E1")])]})]});
            var Q15;
            Q15=makeQuery(id+"F5.boolean.opBoolean","INTERSECT",EDGE,{"disambiguationData":[OD(1.0)],"derivedFrom":[makeQuery(id+"F1.opExtrude","SWEPT_FACE",FACE,{"disambiguationData":[OSD([sQuery(id+"F0.wireOp",EDGE,"E1")])]}),makeQuery(id+"F5.opExtrude","SWEPT_FACE",FACE,{"disambiguationData":[OSD([sQuery(id+"F4.wireOp",EDGE,"E38.MirrorCS")])]})]});
            var Q16;
            {var subQ2=sQuery(id+"F0.wireOp",EDGE,"E5");var subQ3=sQuery(id+"F0.wireOp",EDGE,"E1");var subQ7=sQuery(id+"F0.wireOp",EDGE,"E10.MirrorCS");var subQ9=makeQuery(id+"F5.opExtrude","SWEPT_FACE",FACE,{"disambiguationData":[OSD([sQuery(id+"F4.wireOp",EDGE,"E38.MirrorCS")])]});Q16=makeQuery(id+"F8.opFillet","BLEND_EDGE",EDGE,{"blendedFrom":[makeQuery(id+"F5.boolean.opBoolean","SPLIT",EDGE,{"disambiguationData":[TD([subQ9])],"derivedFrom":makeQuery(id+"F1.opExtrude","SWEPT_EDGE",EDGE,{"disambiguationData":[OSD([subQ3,subQ7])]})}),makeQuery(id+"F5.boolean.opBoolean","COPY",FACE,{"disambiguationData":[TD([makeQuery(id+"F1.opExtrude","SWEPT_FACE",FACE,{"disambiguationData":[OSD([subQ2])]})])],"derivedFrom":subQ9})],"blendedInto":[makeQuery(id+"F5.boolean.opBoolean","COPY",FACE,{"disambiguationData":[TD([makeQuery(id+"F1.opExtrude","SWEPT_FACE",FACE,{"disambiguationData":[OSD([subQ2])]})])],"derivedFrom":subQ9})]});}
            var Q17;
            Q17=makeQuery(id+"F5.boolean.opBoolean","INTERSECT",EDGE,{"derivedFrom":[makeQuery(id+"F1.opExtrude","SWEPT_FACE",FACE,{"disambiguationData":[OSD([sQuery(id+"F0.wireOp",EDGE,"E10.MirrorCS")])]}),makeQuery(id+"F5.opExtrude","SWEPT_FACE",FACE,{"disambiguationData":[OSD([sQuery(id+"F4.wireOp",EDGE,"E38.MirrorCS")])]})]});
            fillet(context, id + "F10", {"entities" : qUnion([Q0, Q1, Q2, Q3, Q4, Q5, Q6, Q7, Q8, Q9, Q10, Q11, Q12, Q13, Q14, Q15, Q16, Q17]), "radius" : 0.5 * mm, "tangentPropagation" : true, "allowEdgeOverflow" : false});
        }
    });
